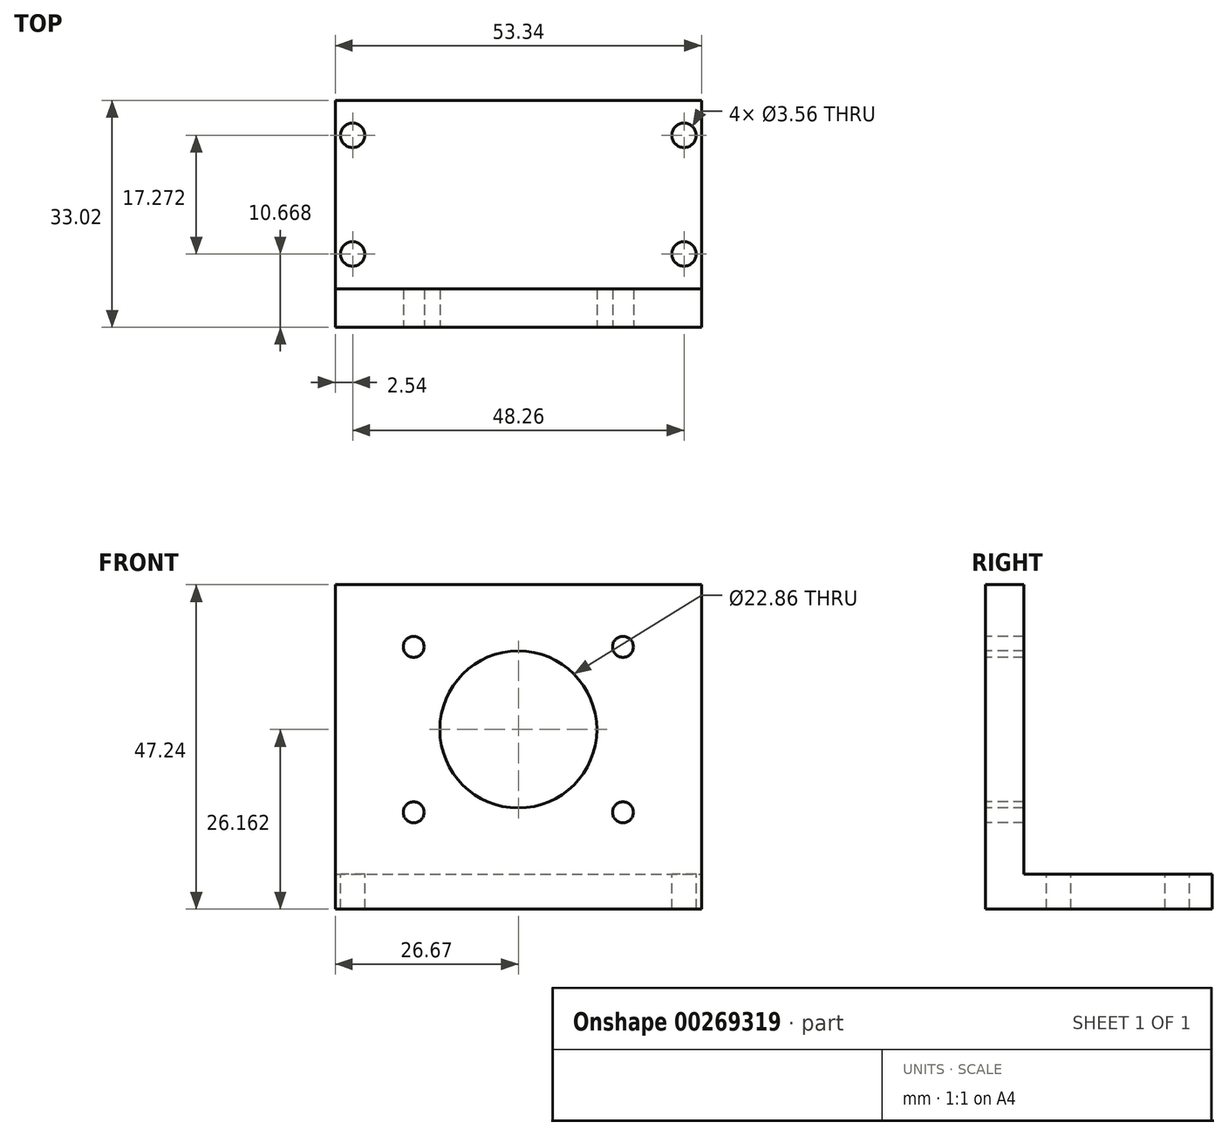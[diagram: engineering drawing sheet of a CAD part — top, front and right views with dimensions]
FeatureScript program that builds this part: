
annotation { "Feature Type Name" : "Feature", "Feature Type Description" : "" }
export const myFeature = defineFeature(function(context is Context, id is Id, definition is map)
    precondition{}
    {
        {
            var Q0;
            Q0=qCreatedBy(makeId("Top.planeOp"),FACE);
            var sketch = newSketch(context, id + "F0", { "sketchPlane" : qUnion([Q0])});
            skLineSegment(sketch, "E0.bottom", {"start": v(0, 0) * mm, "end": v(53.34, 0) * mm});
            skLineSegment(sketch, "E0.top", {"start": v(0, 33.02) * mm, "end": v(53.34, 33.02) * mm});
            skLineSegment(sketch, "E0.left", {"start": v(0, 0) * mm, "end": v(0, 33.02) * mm});
            skLineSegment(sketch, "E0.right", {"start": v(53.34, 0) * mm, "end": v(53.34, 33.02) * mm});
            skLineSegment(sketch, "E1", {"start": v(0, 5.59) * mm, "end": v(53.34, 5.59) * mm});
            skCircle(sketch, "E2", {"center": v(2.54, 27.94) * mm, "radius": 1.78 * mm});
            skCircle(sketch, "E3", {"center": v(2.54, 10.67) * mm, "radius": 1.78 * mm});
            skLineSegment(sketch, "E4", {"start": v(26.67, 33.02) * mm, "end": v(26.67, 5.59) * mm, "construction": true});
            skCircle(sketch, "E5.MirrorC", {"center": v(50.8, 27.94) * mm, "radius": 1.78 * mm});
            skCircle(sketch, "E6.MirrorC", {"center": v(50.8, 10.67) * mm, "radius": 1.78 * mm});
            skSolve(sketch);
        }
        {
            var Q0;
            Q0 = qSketchRegion(id + "F0", true);
            extrude(context, id + "F1", {"entities" : qUnion([Q0]), "oppositeDirection" : true, "depth" : 5.08 * mm});
        }
        {
            var Q0;
            {var subQ0=sQuery(id+"F0.wireOp",EDGE,"E0.bottom");Q0=makeQuery(id+"F0.imprint","IMPRINT",FACE,{"disambiguationData":[TD([[makeQuery(id+"F0.imprint","IMPRINT",EDGE,{"derivedFrom":subQ0}),1.0]])]});}
            extrude(context, id + "F2", {"entities" : qUnion([Q0]), "operationType" : NewBodyOperationType.ADD, "depth" : 42.16 * mm});
        }
        {
            var Q0;
            {var subQ0=sQuery(id+"F0.wireOp",EDGE,"E0.bottom");Q0=makeQuery(id+"F2.boolean.opBoolean","MERGE",FACE,{"derivedFrom":[makeQuery(id+"F1.opExtrude","SWEPT_FACE",FACE,{"disambiguationData":[OSD([subQ0])]}),makeQuery(id+"F2.opExtrude","SWEPT_FACE",FACE,{"disambiguationData":[OSD([subQ0])]})]});}
            var sketch = newSketch(context, id + "F3", { "sketchPlane" : qUnion([Q0])});
            skLineSegment(sketch, "E7", {"start": v(0, 42.16) * mm, "end": v(53.34, 0) * mm, "construction": true});
            skCircle(sketch, "E8", {"center": v(11.43, 33.13) * mm, "radius": 1.52 * mm});
            skLineSegment(sketch, "E9", {"start": v(26.67, 42.16) * mm, "end": v(26.67, 0) * mm, "construction": true});
            skCircle(sketch, "E10.MirrorC", {"center": v(41.91, 33.13) * mm, "radius": 1.52 * mm});
            skLineSegment(sketch, "E11", {"start": v(26.67, 21.08) * mm, "end": v(53.34, 21.08) * mm, "construction": true});
            skCircle(sketch, "E12.MirrorC", {"center": v(11.43, 9.04) * mm, "radius": 1.52 * mm});
            skCircle(sketch, "E13.MirrorC", {"center": v(41.91, 9.04) * mm, "radius": 1.52 * mm});
            skCircle(sketch, "E14", {"center": v(26.67, 21.08) * mm, "radius": 11.43 * mm});
            skSolve(sketch);
        }
        {
            var Q0;
            Q0 = qSketchRegion(id + "F3", true);
            extrude(context, id + "F4", {"entities" : qUnion([Q0]), "operationType" : NewBodyOperationType.REMOVE, "oppositeDirection" : true, "depth" : 25.4 * mm});
        }
    });
